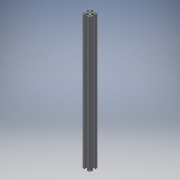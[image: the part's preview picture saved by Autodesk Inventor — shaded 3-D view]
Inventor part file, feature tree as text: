
AUTODESK INVENTOR PART (.ipt)
format: ipt  version: 2018.3 (Build 223284000, 284)  size: 2,146,304 bytes
history: native  units: mm
features: sketch x6, extrude x6, projected_geometry x5, other x3, plane x1, reference x1, fillet x1
ambient origin geometry x8: Origin, YZ Plane, XZ Plane, XY Plane, X Axis, Y Axis, Z Axis, Center Point
bodies: Solid1 (feature_tree)
feature tree (23):
  sketch  "Sketch1"  dims[d0=10.0mm d1=0.0mm d2=165.1mm d3=0.0mm]
  plane  "Work Plane1"
  extrude  "Extrusion1"  Depth=165.1mm TaperAngle=0.0deg
  sketch  "Sketch2"  dims[d4=6.35mm d5=0.0mm d6=17.78mm d7=0.0mm]
  extrude  "Extrusion2"  Depth=17.78mm TaperAngle=0.0deg
  extrude  "Extrusion3"  Depth=10.16mm TaperAngle=0.0deg
  extrude  "Extrusion4"  [1 undecoded]
  extrude  "Extrusion5"  [1 undecoded]
  extrude  "Extrusion6"  [1 undecoded]
  projected_geometry  "Projected Loop1"
  projected_geometry  "Projected Loop2"
  sketch  "Sketch3"  dims[d8=-1184.54mm d9=0.0mm d10=10.16mm d11=0.0mm]
  projected_geometry  "Projected Loop3"
  sketch  "Sketch4"
  projected_geometry  "Projected Loop4"
  sketch  "Sketch5"
  reference  "Reference1"
  sketch  "Sketch6"
  projected_geometry  "Projected Loop5"
  fillet  "Fillet6"  [1 undecoded]
  other  "<userpath>\3D Objects\chassis.iam"
  other  "chassis.iam"
  other  "2 inch rev:2"
note: 4 required parameter values undecoded (feature->parameter linkage not recoverable at this tier; creation-order binding heuristic only, values carry confidence <= 0.55)
